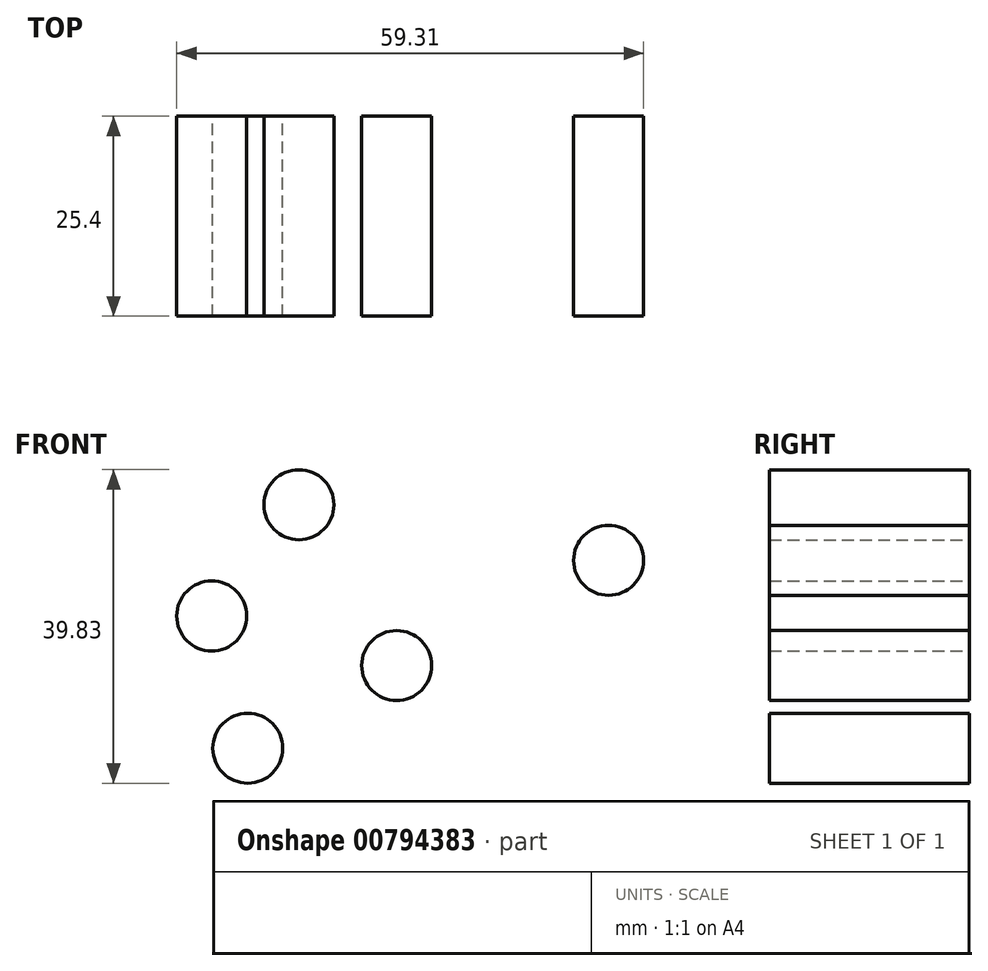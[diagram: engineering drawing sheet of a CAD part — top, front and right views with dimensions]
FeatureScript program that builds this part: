
annotation { "Feature Type Name" : "Feature", "Feature Type Description" : "" }
export const myFeature = defineFeature(function(context is Context, id is Id, definition is map)
    precondition{}
    {
        {
            var Q0;
            Q0=qCreatedBy(makeId("Front.planeOp"),FACE);
            var sketch = newSketch(context, id + "F0", { "sketchPlane" : qUnion([Q0])});
            skCircle(sketch, "E0", {"center": v(-33.7, 23.01) * mm, "radius": 4.45 * mm});
            skCircle(sketch, "E1", {"center": v(-6.78, 36.38) * mm, "radius": 4.45 * mm});
            skCircle(sketch, "E2", {"center": v(-46.12, 43.44) * mm, "radius": 4.45 * mm});
            skCircle(sketch, "E3", {"center": v(-57.2, 29.31) * mm, "radius": 4.45 * mm});
            skCircle(sketch, "E4", {"center": v(-52.6, 12.5) * mm, "radius": 4.45 * mm});
            skSolve(sketch);
        }
        {
            var Q0;
            Q0 = qSketchRegion(id + "F0", true);
            extrude(context, id + "F1", {"entities" : qUnion([Q0]), "depth" : 25.4 * mm, "offsetDistance" : 25.4 * mm});
        }
    });
